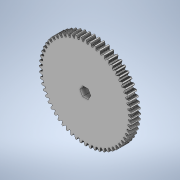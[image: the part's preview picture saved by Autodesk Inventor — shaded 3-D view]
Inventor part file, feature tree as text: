
AUTODESK INVENTOR PART (.ipt)
format: ipt  version: 2022 (Build 260153000, 153)  size: 3,831,296 bytes
history: native  units: mm
features: sketch x2, extrude x2
ambient origin geometry x8: Origin, YZ Plane, XZ Plane, XY Plane, X Axis, Y Axis, Z Axis, Center Point
bodies: Solid1 (feature_tree)
feature tree (4):
  sketch  "Sketch1"  dims[d0=6.2mm d1=0.0mm d20=3.1mm]
  extrude  "Extrusion1"  Depth=6.2mm
  extrude  "Extrusion7"  Depth=0.5mm
  sketch  "Sketch4"  dims[d21=60.0mm d23=360.0deg d34=0.5mm d35=10.0mm d36=0.0mm]
